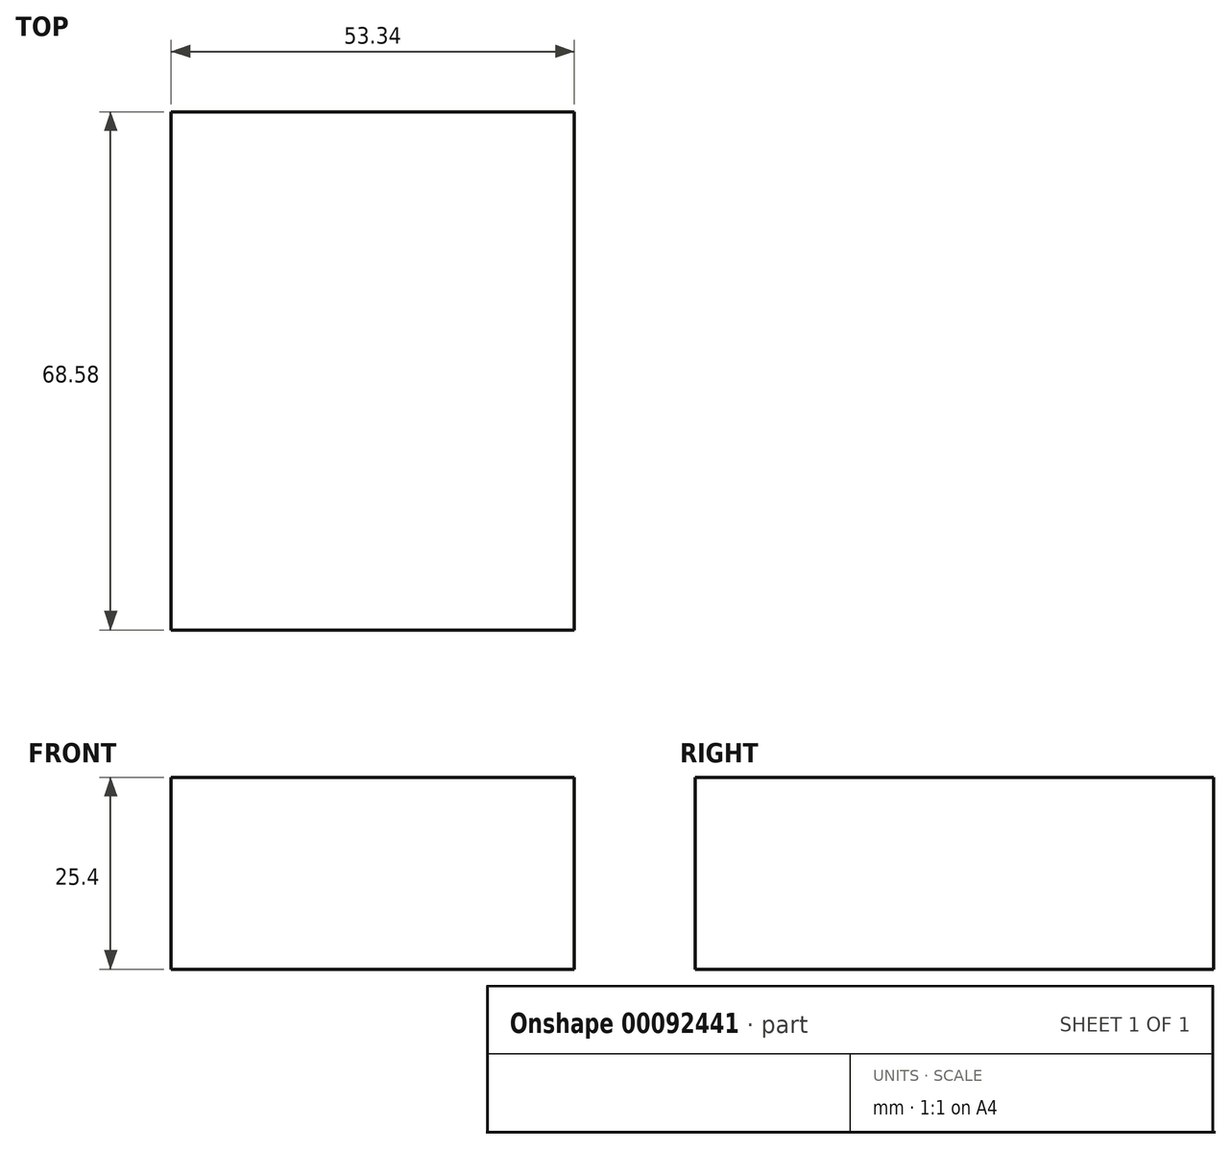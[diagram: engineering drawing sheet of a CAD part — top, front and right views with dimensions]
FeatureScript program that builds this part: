
annotation { "Feature Type Name" : "Feature", "Feature Type Description" : "" }
export const myFeature = defineFeature(function(context is Context, id is Id, definition is map)
    precondition{}
    {
        {
            var Q0;
            Q0=qCreatedBy(makeId("Top.planeOp"),FACE);
            var sketch = newSketch(context, id + "F0", { "sketchPlane" : qUnion([Q0])});
            skLineSegment(sketch, "E0.bottom", {"start": v(27.5, -14.52) * mm, "end": v(-25.85, -14.52) * mm});
            skLineSegment(sketch, "E0.top", {"start": v(27.5, 54.06) * mm, "end": v(-25.85, 54.06) * mm});
            skLineSegment(sketch, "E0.left", {"start": v(27.5, -14.52) * mm, "end": v(27.5, 54.06) * mm});
            skLineSegment(sketch, "E0.right", {"start": v(-25.85, -14.52) * mm, "end": v(-25.85, 54.06) * mm});
            skSolve(sketch);
        }
        {
            var Q0;
            Q0=makeQuery(id+"F0.imprint","IMPRINT",FACE,{"disambiguationData":[TD([[makeQuery(id+"F0.imprint","IMPRINT",EDGE,{"derivedFrom":sQuery(id+"F0.wireOp",EDGE,"E0.bottom")}),-1.0]])]});
            extrude(context, id + "F1", {"entities" : qUnion([Q0]), "depth" : 25.4 * mm});
        }
    });
